# Revit family: HUNTER_WSS-SEN
name_source: partatom
category: Electrical Fixtures
revit_build: Autodesk Revit 2017 (Build: 20190508_0315(x64)
units: mm (PartAtom-declared; Revit-internal decimal feet)

## family parameters
Cut with Voids When Loaded = No
Host = Face
Maintain Annotation Orientation = No
OmniClass Number = 23.27.11.11.23
Part Type = Normal
Room Calculation Point = No
Round Connector Dimension = Use Diameter
Shared = Yes

## types (1)
- WSS-SEN
    Assembly Code = G4030100
    Default Elevation = 1219 mm
    Description = SOLAR-SYNC® Advanced Wireless weather sensor
    Distance Coverage = 240000 mm  [stored 787.402 ft]
    Frequency = 433000000 Hz
    Keynote = 32 84 23.05
    Manufacturer = Hunter® Industries
    Model = WSS-SEN
    Power = 72 VA
    SOLAR-SYNC® Model = Wireless Solar-Sync Sensor
    Sensor Coverage Zone = Yes
    Sensor Depth = 25 mm  [stored 0.082021 ft]
    Sensor Height = 110 mm  [stored 0.360892 ft]
    Sensor Symbol = Yes
    Sensor Width = 220 mm  [stored 0.721785 ft]
    Sensor Wiring = Wireless Sensor
    Type Comments = WSS-SEN® Sensor
    URL = https://www.hunterindustries.com
    WireType_Range_15_30_Meter = 18000 mm
    Wireless = Wireless
    Wireless Antenna = Yes

note: [stored X ft] marks values corroborated as IEEE doubles in the binary element streams (Revit-internal decimal feet)

## geometry (parser evidence)
native form markers: Sweep x11
no freeform markers — native parametric forms only
